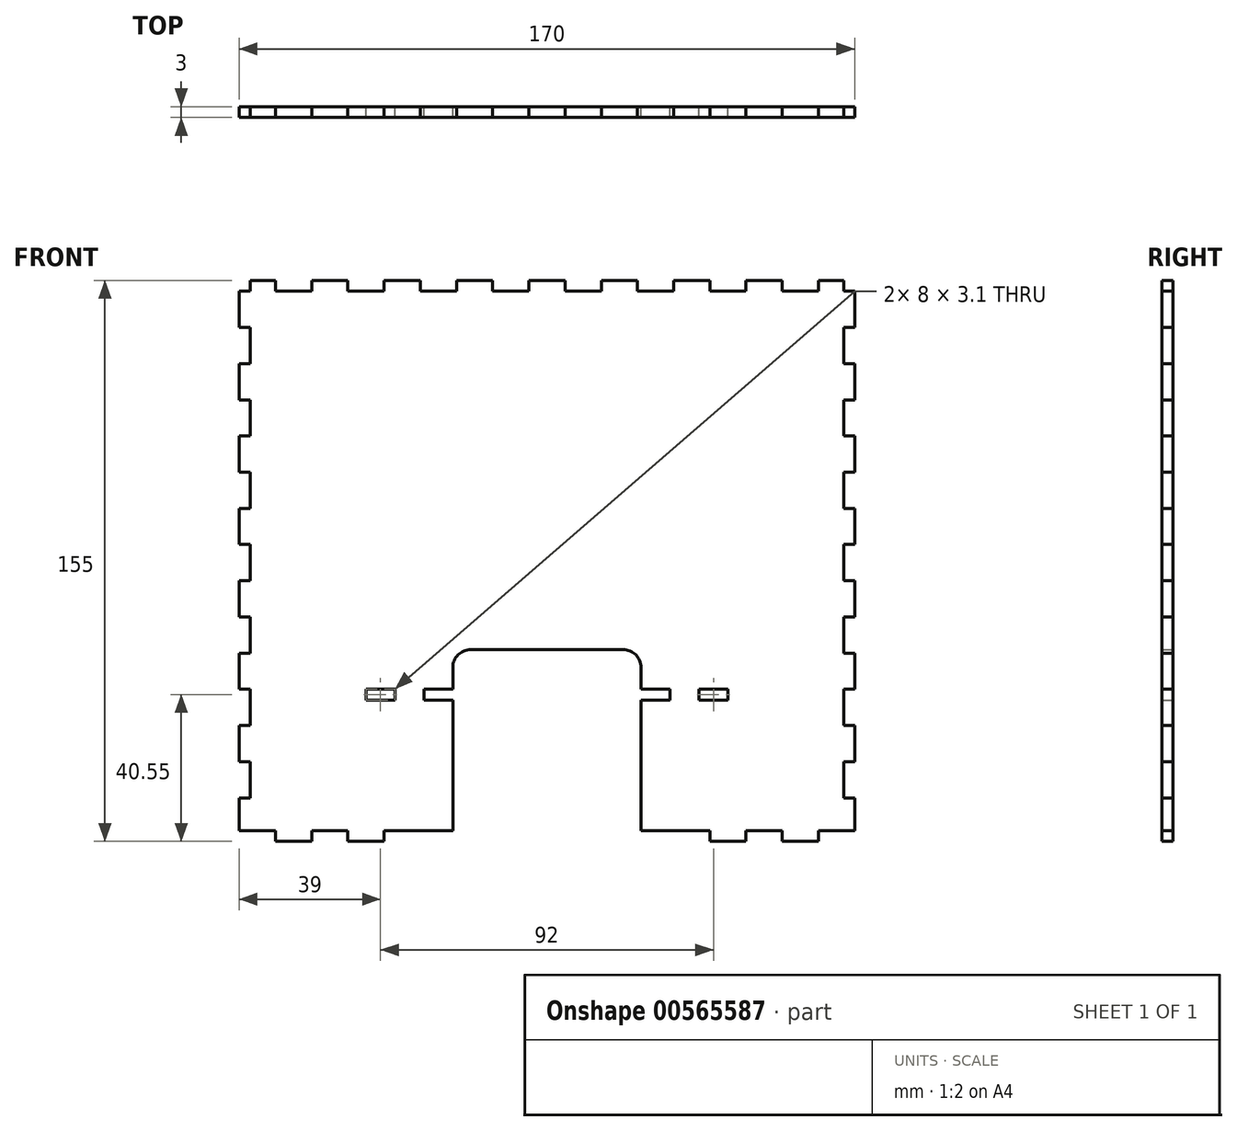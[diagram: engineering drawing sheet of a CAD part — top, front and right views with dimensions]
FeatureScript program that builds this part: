
annotation { "Feature Type Name" : "Feature", "Feature Type Description" : "" }
export const myFeature = defineFeature(function(context is Context, id is Id, definition is map)
    precondition{}
    {
        {
            var Q0;
            Q0=qCreatedBy(makeId("Top.planeOp"),FACE);
            var sketch = newSketch(context, id + "F0", { "sketchPlane" : qUnion([Q0])});
            skLineSegment(sketch, "E0.bottom", {"start": v(82, -30) * mm, "end": v(-82, -30) * mm});
            skLineSegment(sketch, "E0.left", {"start": v(85, -21) * mm, "end": v(85, -13) * mm});
            skLineSegment(sketch, "E0.right", {"start": v(-85, -21) * mm, "end": v(-85, -13) * mm});
            skLineSegment(sketch, "E1.bottom", {"start": v(-85, 21) * mm, "end": v(-82, 21) * mm});
            skLineSegment(sketch, "E1.right", {"start": v(-82, 21) * mm, "end": v(-82, 27) * mm});
            skLineSegment(sketch, "E2.bottom", {"start": v(-85, 13) * mm, "end": v(-82, 13) * mm});
            skLineSegment(sketch, "E2.top", {"start": v(-85, 4) * mm, "end": v(-82, 4) * mm});
            skLineSegment(sketch, "E2.right", {"start": v(-82, 13) * mm, "end": v(-82, 4) * mm});
            skLineSegment(sketch, "E3.bottom", {"start": v(-85, -4) * mm, "end": v(-82, -4) * mm});
            skLineSegment(sketch, "E3.top", {"start": v(-85, -13) * mm, "end": v(-82, -13) * mm});
            skLineSegment(sketch, "E3.right", {"start": v(-82, -4) * mm, "end": v(-82, -13) * mm});
            skLineSegment(sketch, "E4.bottom", {"start": v(-85, -21) * mm, "end": v(-82, -21) * mm});
            skLineSegment(sketch, "E4.right", {"start": v(-82, -21) * mm, "end": v(-82, -30) * mm});
            skLineSegment(sketch, "E5.MirrorCS", {"start": v(85, -13) * mm, "end": v(82, -13) * mm});
            skLineSegment(sketch, "E6.MirrorCS", {"start": v(85, 4) * mm, "end": v(82, 4) * mm});
            skLineSegment(sketch, "E7.MirrorCS", {"start": v(85, -21) * mm, "end": v(82, -21) * mm});
            skLineSegment(sketch, "E8.MirrorCS", {"start": v(85, 13) * mm, "end": v(82, 13) * mm});
            skLineSegment(sketch, "E9.MirrorCS", {"start": v(85, 21) * mm, "end": v(82, 21) * mm});
            skLineSegment(sketch, "E10.MirrorCS", {"start": v(85, -4) * mm, "end": v(82, -4) * mm});
            skLineSegment(sketch, "E11.MirrorCS", {"start": v(82, -21) * mm, "end": v(82, -30) * mm});
            skLineSegment(sketch, "E12.MirrorCS", {"start": v(82, 13) * mm, "end": v(82, 4) * mm});
            skLineSegment(sketch, "E13.MirrorCS", {"start": v(82, -4) * mm, "end": v(82, -13) * mm});
            skLineSegment(sketch, "E14.MirrorCS", {"start": v(82, 21) * mm, "end": v(82, 27) * mm});
            skLineSegment(sketch, "E15.top", {"start": v(-82, 27) * mm, "end": v(-75, 27) * mm});
            skLineSegment(sketch, "E15.right", {"start": v(-75, 30) * mm, "end": v(-75, 27) * mm});
            skLineSegment(sketch, "E16.top", {"start": v(82, 27) * mm, "end": v(75, 27) * mm});
            skLineSegment(sketch, "E16.right", {"start": v(75, 30) * mm, "end": v(75, 27) * mm});
            skLineSegment(sketch, "E17.bottom", {"start": v(65, 27) * mm, "end": v(55, 27) * mm});
            skLineSegment(sketch, "E17.left", {"start": v(65, 27) * mm, "end": v(65, 30) * mm});
            skLineSegment(sketch, "E17.right", {"start": v(55, 27) * mm, "end": v(55, 30) * mm});
            skLineSegment(sketch, "E18.bottom", {"start": v(45, 27) * mm, "end": v(35, 27) * mm});
            skLineSegment(sketch, "E18.left", {"start": v(45, 27) * mm, "end": v(45, 30) * mm});
            skLineSegment(sketch, "E18.right", {"start": v(35, 27) * mm, "end": v(35, 30) * mm});
            skLineSegment(sketch, "E19.bottom", {"start": v(25, 27) * mm, "end": v(15, 27) * mm});
            skLineSegment(sketch, "E19.left", {"start": v(25, 27) * mm, "end": v(25, 30) * mm});
            skLineSegment(sketch, "E19.right", {"start": v(15, 27) * mm, "end": v(15, 30) * mm});
            skLineSegment(sketch, "E20.bottom", {"start": v(5, 27) * mm, "end": v(-5, 27) * mm});
            skLineSegment(sketch, "E20.left", {"start": v(5, 27) * mm, "end": v(5, 30) * mm});
            skLineSegment(sketch, "E20.right", {"start": v(-5, 27) * mm, "end": v(-5, 30) * mm});
            skLineSegment(sketch, "E21.bottom", {"start": v(-15, 27) * mm, "end": v(-25, 27) * mm});
            skLineSegment(sketch, "E21.left", {"start": v(-15, 27) * mm, "end": v(-15, 30) * mm});
            skLineSegment(sketch, "E21.right", {"start": v(-25, 27) * mm, "end": v(-25, 30) * mm});
            skLineSegment(sketch, "E22.bottom", {"start": v(-35, 27) * mm, "end": v(-45, 27) * mm});
            skLineSegment(sketch, "E22.left", {"start": v(-35, 27) * mm, "end": v(-35, 30) * mm});
            skLineSegment(sketch, "E22.right", {"start": v(-45, 27) * mm, "end": v(-45, 30) * mm});
            skLineSegment(sketch, "E23.bottom", {"start": v(-55, 27) * mm, "end": v(-65, 27) * mm});
            skLineSegment(sketch, "E23.left", {"start": v(-55, 27) * mm, "end": v(-55, 30) * mm});
            skLineSegment(sketch, "E23.right", {"start": v(-65, 27) * mm, "end": v(-65, 30) * mm});
            skLineSegment(sketch, "E24.trimOffspring", {"start": v(-85, -4) * mm, "end": v(-85, 4) * mm});
            skLineSegment(sketch, "E25.trimOffspring", {"start": v(-85, 13) * mm, "end": v(-85, 21) * mm});
            skLineSegment(sketch, "E26.trimOffspring", {"start": v(75, 30) * mm, "end": v(65, 30) * mm});
            skLineSegment(sketch, "E27.trimOffspring", {"start": v(-65, 30) * mm, "end": v(-75, 30) * mm});
            skLineSegment(sketch, "E28.trimOffspring", {"start": v(-45, 30) * mm, "end": v(-55, 30) * mm});
            skLineSegment(sketch, "E29.trimOffspring", {"start": v(-25, 30) * mm, "end": v(-35, 30) * mm});
            skLineSegment(sketch, "E30.trimOffspring", {"start": v(-5, 30) * mm, "end": v(-15, 30) * mm});
            skLineSegment(sketch, "E31.trimOffspring", {"start": v(15, 30) * mm, "end": v(5, 30) * mm});
            skLineSegment(sketch, "E32.trimOffspring", {"start": v(35, 30) * mm, "end": v(25, 30) * mm});
            skLineSegment(sketch, "E33.trimOffspring", {"start": v(55, 30) * mm, "end": v(45, 30) * mm});
            skLineSegment(sketch, "E34.trimOffspring", {"start": v(85, 13) * mm, "end": v(85, 21) * mm});
            skLineSegment(sketch, "E35.trimOffspring", {"start": v(85, -4) * mm, "end": v(85, 4) * mm});
            skSolve(sketch);
        }
        {
            var Q0;
            Q0=qCreatedBy(makeId("Front.planeOp"),FACE);
            var sketch = newSketch(context, id + "F1", { "sketchPlane" : qUnion([Q0])});
            skLineSegment(sketch, "E36.bottom", {"start": v(82, 3) * mm, "end": v(75, 3) * mm});
            skLineSegment(sketch, "E36.top", {"start": v(75, -152) * mm, "end": v(65, -152) * mm});
            skLineSegment(sketch, "E36.left", {"start": v(85, 0) * mm, "end": v(85, -10) * mm});
            skLineSegment(sketch, "E36.right", {"start": v(-85, 0) * mm, "end": v(-85, -10) * mm});
            skLineSegment(sketch, "E37.top", {"start": v(82, 0) * mm, "end": v(85, 0) * mm});
            skLineSegment(sketch, "E37.left", {"start": v(82, 3) * mm, "end": v(82, 0) * mm});
            skLineSegment(sketch, "E38.bottom", {"start": v(75, 0) * mm, "end": v(65, 0) * mm});
            skLineSegment(sketch, "E38.left", {"start": v(75, 0) * mm, "end": v(75, 3) * mm});
            skLineSegment(sketch, "E38.right", {"start": v(65, 0) * mm, "end": v(65, 3) * mm});
            skLineSegment(sketch, "E39.bottom", {"start": v(55, 0) * mm, "end": v(45, 0) * mm});
            skLineSegment(sketch, "E39.left", {"start": v(55, 0) * mm, "end": v(55, 3) * mm});
            skLineSegment(sketch, "E39.right", {"start": v(45, 0) * mm, "end": v(45, 3) * mm});
            skLineSegment(sketch, "E40.bottom", {"start": v(35, 0) * mm, "end": v(25, 0) * mm});
            skLineSegment(sketch, "E40.left", {"start": v(35, 0) * mm, "end": v(35, 3) * mm});
            skLineSegment(sketch, "E40.right", {"start": v(25, 0) * mm, "end": v(25, 3) * mm});
            skLineSegment(sketch, "E41.bottom", {"start": v(15, 0) * mm, "end": v(5, 0) * mm});
            skLineSegment(sketch, "E41.left", {"start": v(15, 0) * mm, "end": v(15, 3) * mm});
            skLineSegment(sketch, "E41.right", {"start": v(5, 0) * mm, "end": v(5, 3) * mm});
            skLineSegment(sketch, "E42.bottom", {"start": v(-5, 0) * mm, "end": v(-15, 0) * mm});
            skLineSegment(sketch, "E42.left", {"start": v(-5, 0) * mm, "end": v(-5, 3) * mm});
            skLineSegment(sketch, "E42.right", {"start": v(-15, 0) * mm, "end": v(-15, 3) * mm});
            skLineSegment(sketch, "E43.bottom", {"start": v(-25, 0) * mm, "end": v(-35, 0) * mm});
            skLineSegment(sketch, "E43.left", {"start": v(-25, 0) * mm, "end": v(-25, 3) * mm});
            skLineSegment(sketch, "E43.right", {"start": v(-35, 0) * mm, "end": v(-35, 3) * mm});
            skLineSegment(sketch, "E44.bottom", {"start": v(-45, 0) * mm, "end": v(-55, 0) * mm});
            skLineSegment(sketch, "E44.left", {"start": v(-45, 0) * mm, "end": v(-45, 3) * mm});
            skLineSegment(sketch, "E44.right", {"start": v(-55, 0) * mm, "end": v(-55, 3) * mm});
            skLineSegment(sketch, "E45.bottom", {"start": v(-65, 0) * mm, "end": v(-75, 0) * mm});
            skLineSegment(sketch, "E45.left", {"start": v(-65, 0) * mm, "end": v(-65, 3) * mm});
            skLineSegment(sketch, "E45.right", {"start": v(-75, 0) * mm, "end": v(-75, 3) * mm});
            skLineSegment(sketch, "E46.bottom", {"start": v(-82, 0) * mm, "end": v(-85, 0) * mm});
            skLineSegment(sketch, "E46.left", {"start": v(-82, 0) * mm, "end": v(-82, 3) * mm});
            skLineSegment(sketch, "E47.top", {"start": v(21, -99) * mm, "end": v(-21, -99) * mm});
            skLineSegment(sketch, "E47.left", {"start": v(26, -149) * mm, "end": v(26, -113) * mm});
            skLineSegment(sketch, "E47.right", {"start": v(-26, -149) * mm, "end": v(-26, -113) * mm});
            skLineSegment(sketch, "E48.bottom", {"start": v(82, -10) * mm, "end": v(85, -10) * mm});
            skLineSegment(sketch, "E48.top", {"start": v(82, -20) * mm, "end": v(85, -20) * mm});
            skLineSegment(sketch, "E48.left", {"start": v(82, -10) * mm, "end": v(82, -20) * mm});
            skLineSegment(sketch, "E49.bottom", {"start": v(82, -50) * mm, "end": v(85, -50) * mm});
            skLineSegment(sketch, "E49.top", {"start": v(82, -60) * mm, "end": v(85, -60) * mm});
            skLineSegment(sketch, "E49.left", {"start": v(82, -50) * mm, "end": v(82, -60) * mm});
            skLineSegment(sketch, "E50.bottom", {"start": v(82, -70) * mm, "end": v(85, -70) * mm});
            skLineSegment(sketch, "E50.top", {"start": v(82, -80) * mm, "end": v(85, -80) * mm});
            skLineSegment(sketch, "E50.left", {"start": v(82, -70) * mm, "end": v(82, -80) * mm});
            skLineSegment(sketch, "E51.bottom", {"start": v(82, -90) * mm, "end": v(85, -90) * mm});
            skLineSegment(sketch, "E51.top", {"start": v(82, -100) * mm, "end": v(85, -100) * mm});
            skLineSegment(sketch, "E51.left", {"start": v(82, -90) * mm, "end": v(82, -100) * mm});
            skLineSegment(sketch, "E52.bottom", {"start": v(82, -110) * mm, "end": v(85, -110) * mm});
            skLineSegment(sketch, "E52.top", {"start": v(82, -120) * mm, "end": v(85, -120) * mm});
            skLineSegment(sketch, "E52.left", {"start": v(82, -110) * mm, "end": v(82, -120) * mm});
            skLineSegment(sketch, "E53.bottom", {"start": v(82, -130) * mm, "end": v(85, -130) * mm});
            skLineSegment(sketch, "E53.top", {"start": v(82, -140) * mm, "end": v(85, -140) * mm});
            skLineSegment(sketch, "E53.left", {"start": v(82, -130) * mm, "end": v(82, -140) * mm});
            skLineSegment(sketch, "E54.bottom", {"start": v(85, -30) * mm, "end": v(82, -30) * mm});
            skLineSegment(sketch, "E54.top", {"start": v(85, -40) * mm, "end": v(82, -40) * mm});
            skLineSegment(sketch, "E54.right", {"start": v(82, -30) * mm, "end": v(82, -40) * mm});
            skLineSegment(sketch, "E55.MirrorCS", {"start": v(-82, -50) * mm, "end": v(-85, -50) * mm});
            skLineSegment(sketch, "E56.MirrorCS", {"start": v(-82, -120) * mm, "end": v(-85, -120) * mm});
            skLineSegment(sketch, "E57.MirrorCS", {"start": v(-82, -20) * mm, "end": v(-85, -20) * mm});
            skLineSegment(sketch, "E58.MirrorCS", {"start": v(-82, -110) * mm, "end": v(-85, -110) * mm});
            skLineSegment(sketch, "E59.MirrorCS", {"start": v(-82, -130) * mm, "end": v(-85, -130) * mm});
            skLineSegment(sketch, "E60.MirrorCS", {"start": v(-82, -100) * mm, "end": v(-85, -100) * mm});
            skLineSegment(sketch, "E61.MirrorCS", {"start": v(-82, -60) * mm, "end": v(-85, -60) * mm});
            skLineSegment(sketch, "E62.MirrorCS", {"start": v(-85, -30) * mm, "end": v(-82, -30) * mm});
            skLineSegment(sketch, "E63.MirrorCS", {"start": v(-85, -40) * mm, "end": v(-82, -40) * mm});
            skLineSegment(sketch, "E64.MirrorCS", {"start": v(-82, -80) * mm, "end": v(-85, -80) * mm});
            skLineSegment(sketch, "E65.MirrorCS", {"start": v(-82, -90) * mm, "end": v(-85, -90) * mm});
            skLineSegment(sketch, "E66.MirrorCS", {"start": v(-82, -140) * mm, "end": v(-85, -140) * mm});
            skLineSegment(sketch, "E67.MirrorCS", {"start": v(-82, -10) * mm, "end": v(-85, -10) * mm});
            skLineSegment(sketch, "E68.MirrorCS", {"start": v(-82, -70) * mm, "end": v(-85, -70) * mm});
            skLineSegment(sketch, "E69.MirrorCS", {"start": v(-82, -10) * mm, "end": v(-82, -20) * mm});
            skLineSegment(sketch, "E70.MirrorCS", {"start": v(-82, -110) * mm, "end": v(-82, -120) * mm});
            skLineSegment(sketch, "E71.MirrorCS", {"start": v(-82, -50) * mm, "end": v(-82, -60) * mm});
            skLineSegment(sketch, "E72.MirrorCS", {"start": v(-82, -130) * mm, "end": v(-82, -140) * mm});
            skLineSegment(sketch, "E73.MirrorCS", {"start": v(-82, -90) * mm, "end": v(-82, -100) * mm});
            skLineSegment(sketch, "E74.MirrorCS", {"start": v(-82, -70) * mm, "end": v(-82, -80) * mm});
            skLineSegment(sketch, "E75.MirrorCS", {"start": v(-82, -30) * mm, "end": v(-82, -40) * mm});
            skLineSegment(sketch, "E76.top", {"start": v(85, -149) * mm, "end": v(75, -149) * mm});
            skLineSegment(sketch, "E76.right", {"start": v(75, -152) * mm, "end": v(75, -149) * mm});
            skLineSegment(sketch, "E77.bottom", {"start": v(65, -149) * mm, "end": v(55, -149) * mm});
            skLineSegment(sketch, "E77.left", {"start": v(65, -149) * mm, "end": v(65, -152) * mm});
            skLineSegment(sketch, "E77.right", {"start": v(55, -149) * mm, "end": v(55, -152) * mm});
            skLineSegment(sketch, "E78.MirrorCS", {"start": v(-55, -149) * mm, "end": v(-55, -152) * mm});
            skLineSegment(sketch, "E79.MirrorCS", {"start": v(-65, -149) * mm, "end": v(-55, -149) * mm});
            skLineSegment(sketch, "E80.MirrorCS", {"start": v(-65, -149) * mm, "end": v(-65, -152) * mm});
            skLineSegment(sketch, "E81.MirrorCS", {"start": v(-85, -149) * mm, "end": v(-75, -149) * mm});
            skLineSegment(sketch, "E82.MirrorCS", {"start": v(-75, -152) * mm, "end": v(-75, -149) * mm});
            skLineSegment(sketch, "E83.trimOffspring", {"start": v(-85, -20) * mm, "end": v(-85, -30) * mm});
            skPoint(sketch, "E84.MirrorCS.start.orphan", {"position": v(-85, -10) * mm});
            skLineSegment(sketch, "E85.trimOffspring", {"start": v(-75, 3) * mm, "end": v(-82, 3) * mm});
            skLineSegment(sketch, "E86.trimOffspring", {"start": v(-85, -40) * mm, "end": v(-85, -50) * mm});
            skLineSegment(sketch, "E87.trimOffspring", {"start": v(-85, -60) * mm, "end": v(-85, -70) * mm});
            skLineSegment(sketch, "E88.trimOffspring", {"start": v(-55, 3) * mm, "end": v(-65, 3) * mm});
            skLineSegment(sketch, "E89.trimOffspring", {"start": v(-35, 3) * mm, "end": v(-45, 3) * mm});
            skLineSegment(sketch, "E90.trimOffspring", {"start": v(-15, 3) * mm, "end": v(-25, 3) * mm});
            skLineSegment(sketch, "E91.trimOffspring", {"start": v(5, 3) * mm, "end": v(-5, 3) * mm});
            skLineSegment(sketch, "E92.trimOffspring", {"start": v(25, 3) * mm, "end": v(15, 3) * mm});
            skLineSegment(sketch, "E93.trimOffspring", {"start": v(45, 3) * mm, "end": v(35, 3) * mm});
            skLineSegment(sketch, "E94.trimOffspring", {"start": v(65, 3) * mm, "end": v(55, 3) * mm});
            skLineSegment(sketch, "E95.trimOffspring", {"start": v(85, -20) * mm, "end": v(85, -30) * mm});
            skLineSegment(sketch, "E96.trimOffspring", {"start": v(-85, -80) * mm, "end": v(-85, -90) * mm});
            skLineSegment(sketch, "E97.trimOffspring", {"start": v(-85, -100) * mm, "end": v(-85, -110) * mm});
            skLineSegment(sketch, "E98.trimOffspring", {"start": v(-85, -120) * mm, "end": v(-85, -130) * mm});
            skLineSegment(sketch, "E99.trimOffspring", {"start": v(-85, -140) * mm, "end": v(-85, -149) * mm});
            skPoint(sketch, "E100.MirrorCS.start.orphan", {"position": v(-85, -152) * mm});
            skLineSegment(sketch, "E101.trimOffspring", {"start": v(-65, -152) * mm, "end": v(-75, -152) * mm});
            skLineSegment(sketch, "E102.trimOffspring", {"start": v(55, -152) * mm, "end": v(45, -152) * mm});
            skPoint(sketch, "E76.left.start.orphan", {"position": v(85, -152) * mm});
            skLineSegment(sketch, "E103.trimOffspring", {"start": v(85, -140) * mm, "end": v(85, -149) * mm});
            skLineSegment(sketch, "E104.trimOffspring", {"start": v(85, -120) * mm, "end": v(85, -130) * mm});
            skLineSegment(sketch, "E105.trimOffspring", {"start": v(85, -100) * mm, "end": v(85, -110) * mm});
            skLineSegment(sketch, "E106.trimOffspring", {"start": v(85, -80) * mm, "end": v(85, -90) * mm});
            skLineSegment(sketch, "E107.trimOffspring", {"start": v(85, -60) * mm, "end": v(85, -70) * mm});
            skLineSegment(sketch, "E108.trimOffspring", {"start": v(85, -40) * mm, "end": v(85, -50) * mm});
            skLineSegment(sketch, "E109.trimOffspring", {"start": v(-45, -152) * mm, "end": v(-55, -152) * mm});
            skLineSegment(sketch, "E110", {"start": v(26, -149) * mm, "end": v(45, -149) * mm});
            skLineSegment(sketch, "E111", {"start": v(45, -149) * mm, "end": v(45, -152) * mm});
            skLineSegment(sketch, "E112", {"start": v(-26, -149) * mm, "end": v(-45, -149) * mm});
            skLineSegment(sketch, "E113", {"start": v(-45, -149) * mm, "end": v(-45, -152) * mm});
            skPoint(sketch, "E114.orphan", {"position": v(26, -152) * mm});
            skLineSegment(sketch, "E115.bottom", {"start": v(26, -109.9) * mm, "end": v(34, -109.9) * mm});
            skLineSegment(sketch, "E115.top", {"start": v(26, -113) * mm, "end": v(34, -113) * mm});
            skLineSegment(sketch, "E115.right", {"start": v(34, -109.9) * mm, "end": v(34, -113) * mm});
            skLineSegment(sketch, "E116.bottom", {"start": v(42, -113) * mm, "end": v(50, -113) * mm});
            skLineSegment(sketch, "E116.top", {"start": v(42, -109.9) * mm, "end": v(50, -109.9) * mm});
            skLineSegment(sketch, "E116.left", {"start": v(42, -113) * mm, "end": v(42, -109.9) * mm});
            skLineSegment(sketch, "E116.right", {"start": v(50, -113) * mm, "end": v(50, -109.9) * mm});
            skLineSegment(sketch, "E117.bottom", {"start": v(-26, -113) * mm, "end": v(-34, -113) * mm});
            skLineSegment(sketch, "E117.top", {"start": v(-26, -109.9) * mm, "end": v(-34, -109.9) * mm});
            skLineSegment(sketch, "E117.right", {"start": v(-34, -113) * mm, "end": v(-34, -109.9) * mm});
            skLineSegment(sketch, "E118.bottom", {"start": v(-42, -113) * mm, "end": v(-50, -113) * mm});
            skLineSegment(sketch, "E118.top", {"start": v(-42, -109.9) * mm, "end": v(-50, -109.9) * mm});
            skLineSegment(sketch, "E118.left", {"start": v(-42, -113) * mm, "end": v(-42, -109.9) * mm});
            skLineSegment(sketch, "E118.right", {"start": v(-50, -113) * mm, "end": v(-50, -109.9) * mm});
            skPoint(sketch, "E119.visualSharp", {"position": v(26, -99) * mm});
            skArc(sketch, "E119.filletArc", {"start": v(26, -104) * mm, "mid": v(24.54, -100.46) * mm, "end": v(21, -99) * mm});
            skPoint(sketch, "E120.visualSharp", {"position": v(-26, -99) * mm});
            skArc(sketch, "E120.filletArc", {"start": v(-21, -99) * mm, "mid": v(-24.54, -100.46) * mm, "end": v(-26, -104) * mm});
            skLineSegment(sketch, "E121.trimOffspring", {"start": v(26, -109.9) * mm, "end": v(26, -104) * mm});
            skLineSegment(sketch, "E122.trimOffspring", {"start": v(-26, -109.9) * mm, "end": v(-26, -104) * mm});
            skSolve(sketch);
        }
        {
            var Q0;
            {var subQ29=sQuery(id+"F1.wireOp",EDGE,"E36.right");Q0=makeQuery(id+"F1.imprint","IMPRINT",FACE,{"disambiguationData":[TD([[makeQuery(id+"F1.imprint","IMPRINT",EDGE,{"derivedFrom":subQ29}),1.0]])]});}
            extrude(context, id + "F2", {"entities" : qUnion([Q0]), "depth" : 3 * mm, "offsetDistance" : 25 * mm});
        }
    });
